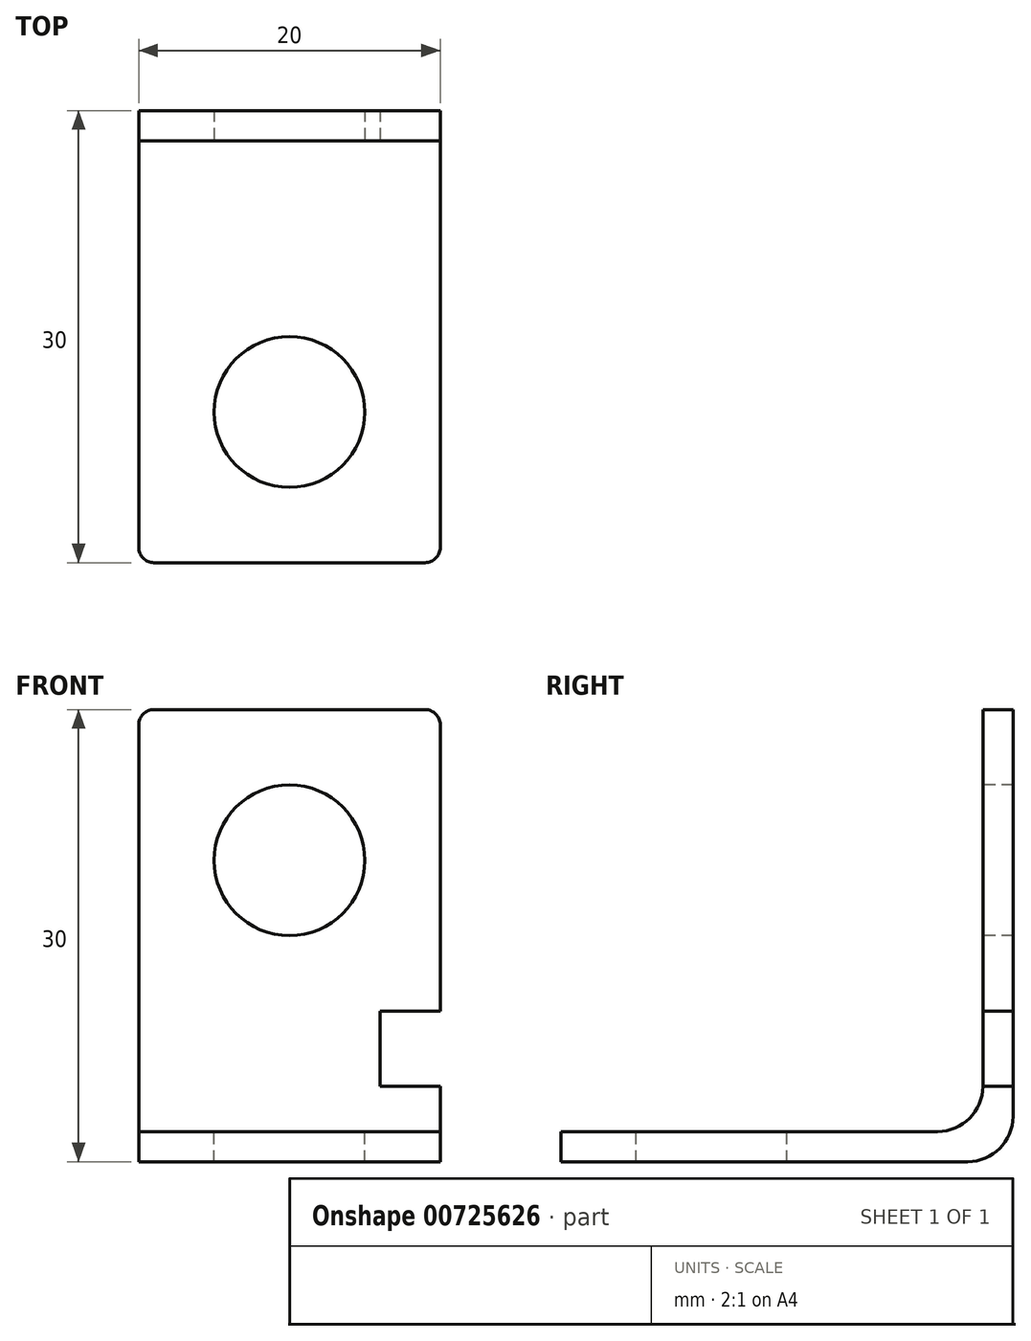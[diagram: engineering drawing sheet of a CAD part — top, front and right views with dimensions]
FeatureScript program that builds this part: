
annotation { "Feature Type Name" : "Feature", "Feature Type Description" : "" }
export const myFeature = defineFeature(function(context is Context, id is Id, definition is map)
    precondition{}
    {
        {
            var Q0;
            Q0=qCreatedBy(makeId("Right.planeOp"),FACE);
            var sketch = newSketch(context, id + "F0", { "sketchPlane" : qUnion([Q0])});
            skLineSegment(sketch, "E0", {"start": v(0, 0) * mm, "end": v(30, 0) * mm});
            skLineSegment(sketch, "E1", {"start": v(30, 0) * mm, "end": v(30, 30) * mm});
            skLineSegment(sketch, "E2.0", {"start": v(28, 2) * mm, "end": v(28, 30) * mm});
            skLineSegment(sketch, "E2.1", {"start": v(0, 2) * mm, "end": v(28, 2) * mm});
            skLineSegment(sketch, "E3", {"start": v(28, 30) * mm, "end": v(30, 30) * mm});
            skLineSegment(sketch, "E4", {"start": v(0, 2) * mm, "end": v(0, 0) * mm});
            skSolve(sketch);
        }
        {
            var Q0;
            Q0=makeQuery(id+"F0.imprint","IMPRINT",FACE,{"disambiguationData":[TD([[makeQuery(id+"F0.imprint","IMPRINT",EDGE,{"derivedFrom":sQuery(id+"F0.wireOp",EDGE,"E0")}),1.0]])]});
            extrude(context, id + "F1", {"entities" : qUnion([Q0]), "depth" : 20 * mm, "offsetDistance" : 25 * mm});
        }
        {
            var Q0;
            Q0=makeQuery(id+"F1.opExtrude","SWEPT_FACE",FACE,{"disambiguationData":[OSD([sQuery(id+"F0.wireOp",EDGE,"E2.0")])]});
            var sketch = newSketch(context, id + "F2", { "sketchPlane" : qUnion([Q0])});
            skCircle(sketch, "E5", {"center": v(10, 20) * mm, "radius": 5 * mm});
            skLineSegment(sketch, "E6.bottom", {"start": v(20, 10) * mm, "end": v(16, 10) * mm});
            skLineSegment(sketch, "E6.top", {"start": v(20, 5) * mm, "end": v(16, 5) * mm});
            skLineSegment(sketch, "E6.left", {"start": v(20, 10) * mm, "end": v(20, 5) * mm});
            skLineSegment(sketch, "E6.right", {"start": v(16, 10) * mm, "end": v(16, 5) * mm});
            skSolve(sketch);
        }
        {
            var Q0;
            Q0 = qSketchRegion(id + "F2", true);
            extrude(context, id + "F3", {"entities" : qUnion([Q0]), "operationType" : NewBodyOperationType.REMOVE, "endBound" : BoundingType.THROUGH_ALL, "oppositeDirection" : true, "depth" : 25 * mm, "offsetDistance" : 25 * mm});
        }
        {
            var Q0;
            Q0=makeQuery(id+"F1.opExtrude","SWEPT_FACE",FACE,{"disambiguationData":[OSD([sQuery(id+"F0.wireOp",EDGE,"E2.1")])]});
            var sketch = newSketch(context, id + "F4", { "sketchPlane" : qUnion([Q0])});
            skCircle(sketch, "E7", {"center": v(10, 10) * mm, "radius": 5 * mm});
            skSolve(sketch);
        }
        {
            var Q0;
            Q0=makeQuery(id+"F4.imprint","IMPRINT",FACE,{"disambiguationData":[TD([[makeQuery(id+"F4.imprint","IMPRINT",EDGE,{"derivedFrom":sQuery(id+"F4.wireOp",EDGE,"E7")}),1.0]])]});
            extrude(context, id + "F5", {"entities" : qUnion([Q0]), "operationType" : NewBodyOperationType.REMOVE, "endBound" : BoundingType.THROUGH_ALL, "oppositeDirection" : true, "depth" : 25 * mm, "offsetDistance" : 25 * mm});
        }
        {
            var Q0;
            Q0=makeQuery(id+"F1.opExtrude","SWEPT_EDGE",EDGE,{"disambiguationData":[OSD([sQuery(id+"F0.wireOp",EDGE,"E2.0"),sQuery(id+"F0.wireOp",EDGE,"E2.1")])]});
            var Q1;
            Q1=makeQuery(id+"F1.opExtrude","SWEPT_EDGE",EDGE,{"disambiguationData":[OSD([sQuery(id+"F0.wireOp",EDGE,"E0"),sQuery(id+"F0.wireOp",EDGE,"E1")])]});
            fillet(context, id + "F6", {"entities" : qUnion([Q0, Q1]), "radius" : 3 * mm, "tangentPropagation" : true, "allowEdgeOverflow" : false});
        }
        {
            var Q0;
            Q0=makeQuery(id+"F1.opExtrude","CAP_EDGE",EDGE,{"disambiguationData":[OSD([sQuery(id+"F0.wireOp",EDGE,"E4")])],"isStart":true});
            var Q1;
            Q1=makeQuery(id+"F1.opExtrude","CAP_EDGE",EDGE,{"disambiguationData":[OSD([sQuery(id+"F0.wireOp",EDGE,"E4")])],"isStart":false});
            var Q2;
            Q2=makeQuery(id+"F1.opExtrude","CAP_EDGE",EDGE,{"disambiguationData":[OSD([sQuery(id+"F0.wireOp",EDGE,"E3")])],"isStart":false});
            var Q3;
            Q3=makeQuery(id+"F1.opExtrude","CAP_EDGE",EDGE,{"disambiguationData":[OSD([sQuery(id+"F0.wireOp",EDGE,"E3")])],"isStart":true});
            fillet(context, id + "F7", {"entities" : qUnion([Q0, Q1, Q2, Q3]), "radius" : 1 * mm, "tangentPropagation" : true, "allowEdgeOverflow" : false});
        }
    });
